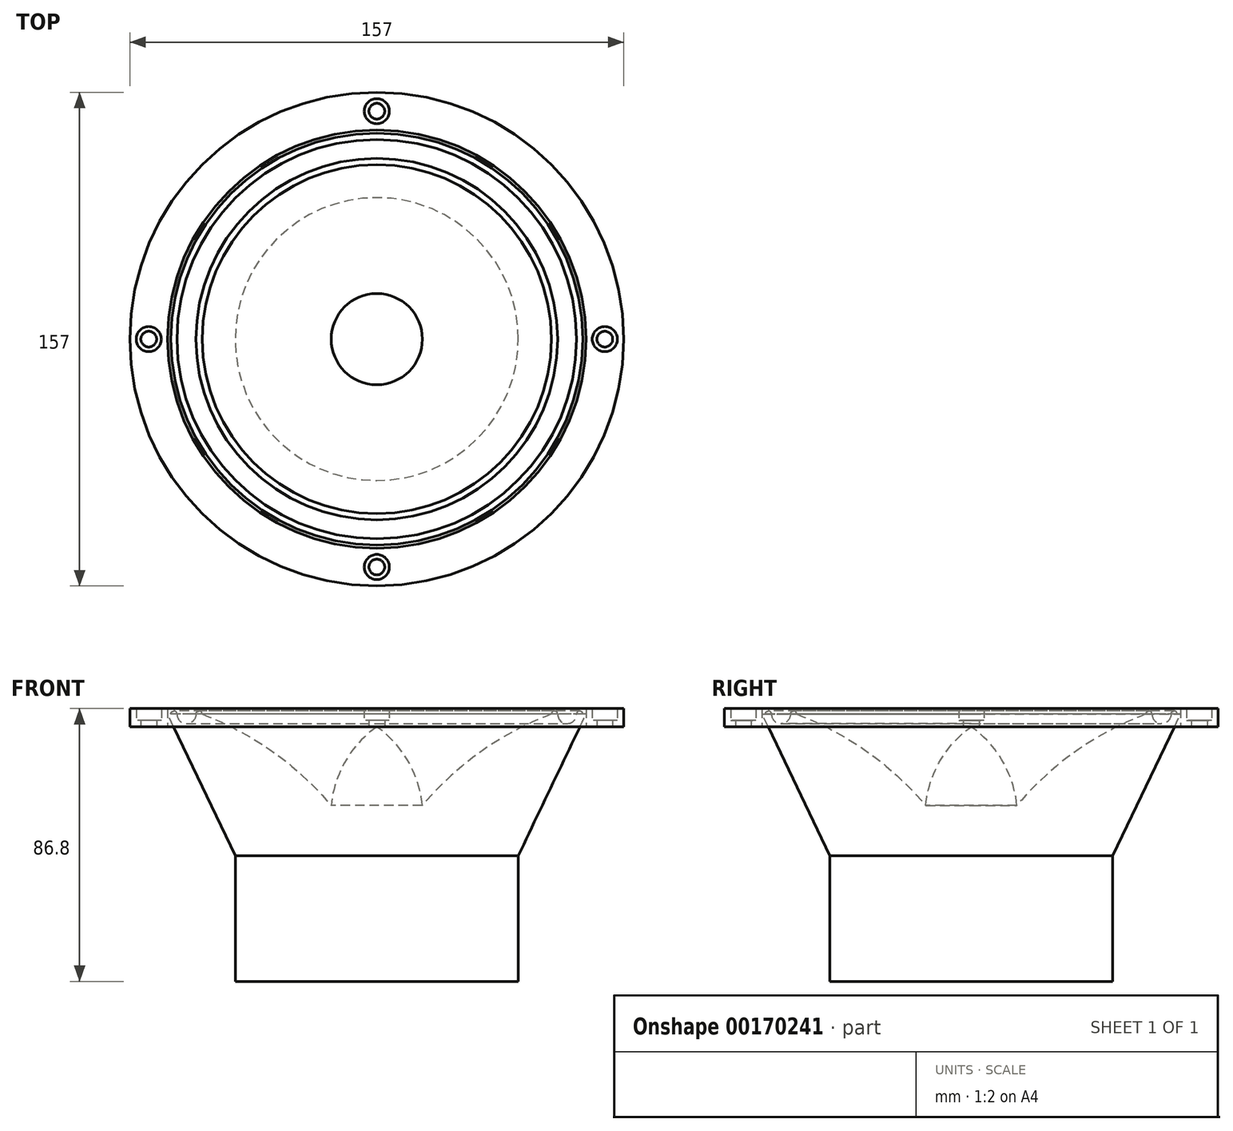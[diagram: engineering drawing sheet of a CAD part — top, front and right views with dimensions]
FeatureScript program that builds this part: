
annotation { "Feature Type Name" : "Feature", "Feature Type Description" : "" }
export const myFeature = defineFeature(function(context is Context, id is Id, definition is map)
    precondition{}
    {
        {
            var Q0;
            Q0=qCreatedBy(makeId("Top.planeOp"),FACE);
            var sketch = newSketch(context, id + "F0", { "sketchPlane" : qUnion([Q0])});
            skCircle(sketch, "E0", {"center": v(0, 0) * mm, "radius": 78.5 * mm});
            skCircle(sketch, "E1", {"center": v(0, 0) * mm, "radius": 72.5 * mm, "construction": true});
            skCircle(sketch, "E2", {"center": v(0, 0) * mm, "radius": 65.5 * mm});
            skCircle(sketch, "E3", {"center": v(0, 72.5) * mm, "radius": 2.5 * mm});
            skCircle(sketch, "E4", {"center": v(0, 72.5) * mm, "radius": 4 * mm});
            skLineSegment(sketch, "E5", {"start": v(0, 0) * mm, "end": v(0, 72.5) * mm, "construction": true});
            skCircle(sketch, "E6.1.0", {"center": v(-72.5, 0) * mm, "radius": 2.5 * mm});
            skCircle(sketch, "E6.1.1", {"center": v(-72.5, 0) * mm, "radius": 4 * mm});
            skCircle(sketch, "E6.2.0", {"center": v(0, -72.5) * mm, "radius": 2.5 * mm});
            skCircle(sketch, "E6.2.1", {"center": v(0, -72.5) * mm, "radius": 4 * mm});
            skCircle(sketch, "E7.1.3.0", {"center": v(72.5, 0) * mm, "radius": 2.5 * mm});
            skCircle(sketch, "E7.2.3.0", {"center": v(72.5, 0) * mm, "radius": 4 * mm});
            skLineSegment(sketch, "E8", {"start": v(0, 78.5) * mm, "end": v(0, 66.5) * mm, "construction": true});
            skCircle(sketch, "E9", {"center": v(0, 0) * mm, "radius": 66.5 * mm});
            skCircle(sketch, "E10", {"center": v(0, 0) * mm, "radius": 63.5 * mm});
            skCircle(sketch, "E11", {"center": v(0, 0) * mm, "radius": 57.5 * mm});
            skCircle(sketch, "E12", {"center": v(0, 0) * mm, "radius": 55.5 * mm});
            skCircle(sketch, "E13", {"center": v(0, 0) * mm, "radius": 14.5 * mm});
            skCircle(sketch, "E14", {"center": v(0, 0) * mm, "radius": 12.5 * mm});
            skSolve(sketch);
        }
        {
            var Q0;
            Q0=makeQuery(id+"F0.imprint","IMPRINT",FACE,{"disambiguationData":[TD([[makeQuery(id+"F0.imprint","IMPRINT",EDGE,{"derivedFrom":sQuery(id+"F0.wireOp",EDGE,"E0")}),1.0]])]});
            extrude(context, id + "F1", {"entities" : qUnion([Q0]), "depth" : 5.8 * mm});
        }
        {
            var Q0;
            Q0=makeQuery(id+"F0.imprint","IMPRINT",FACE,{"disambiguationData":[TD([[makeQuery(id+"F0.imprint","IMPRINT",EDGE,{"derivedFrom":sQuery(id+"F0.wireOp",EDGE,"E6.2.0")}),-1.0]])]});
            var Q1;
            Q1=makeQuery(id+"F0.imprint","IMPRINT",FACE,{"disambiguationData":[TD([[makeQuery(id+"F0.imprint","IMPRINT",EDGE,{"derivedFrom":sQuery(id+"F0.wireOp",EDGE,"E6.1.0")}),-1.0]])]});
            var Q2;
            Q2=makeQuery(id+"F0.imprint","IMPRINT",FACE,{"disambiguationData":[TD([[makeQuery(id+"F0.imprint","IMPRINT",EDGE,{"derivedFrom":sQuery(id+"F0.wireOp",EDGE,"E3")}),-1.0]])]});
            var Q3;
            Q3=makeQuery(id+"F0.imprint","IMPRINT",FACE,{"disambiguationData":[TD([[makeQuery(id+"F0.imprint","IMPRINT",EDGE,{"derivedFrom":sQuery(id+"F0.wireOp",EDGE,"E7.1.3.0")}),-1.0]])]});
            extrude(context, id + "F2", {"entities" : qUnion([Q0, Q1, Q2, Q3]), "operationType" : NewBodyOperationType.ADD, "depth" : 2 * mm});
        }
        {
            var Q0;
            Q0=qCreatedBy(makeId("Right.planeOp"),FACE);
            var sketch = newSketch(context, id + "F3", { "sketchPlane" : qUnion([Q0])});
            skLineSegment(sketch, "E15.0", {"start": v(-65.5, 0) * mm, "end": v(65.5, 0) * mm, "construction": true});
            skLineSegment(sketch, "E16.0", {"start": v(-63.5, 0) * mm, "end": v(63.5, 0) * mm, "construction": true});
            skLineSegment(sketch, "E17.0", {"start": v(-57.5, 0) * mm, "end": v(57.5, 0) * mm, "construction": true});
            skLineSegment(sketch, "E18.0", {"start": v(-55.5, 0) * mm, "end": v(55.5, 0) * mm, "construction": true});
            skLineSegment(sketch, "E19", {"start": v(-65.5, 0) * mm, "end": v(-65.5, 4) * mm, "construction": true});
            skLineSegment(sketch, "E20", {"start": v(-65.5, 4) * mm, "end": v(65.5, 4) * mm, "construction": true});
            skLineSegment(sketch, "E21", {"start": v(65.5, 4) * mm, "end": v(65.5, 0) * mm, "construction": true});
            skLineSegment(sketch, "E22", {"start": v(-63.5, 0) * mm, "end": v(-63.5, 4) * mm, "construction": true});
            skLineSegment(sketch, "E23", {"start": v(-57.5, 0) * mm, "end": v(-57.5, 4) * mm, "construction": true});
            skLineSegment(sketch, "E24", {"start": v(-55.5, 0) * mm, "end": v(-55.5, 4) * mm, "construction": true});
            skLineSegment(sketch, "E25", {"start": v(63.5, 0) * mm, "end": v(63.5, 4) * mm, "construction": true});
            skLineSegment(sketch, "E26", {"start": v(57.5, 0) * mm, "end": v(57.5, 4) * mm, "construction": true});
            skLineSegment(sketch, "E27", {"start": v(55.5, 0) * mm, "end": v(55.5, 4) * mm, "construction": true});
            skLineSegment(sketch, "E28.0", {"start": v(-14.5, 0) * mm, "end": v(14.5, 0) * mm});
            skLineSegment(sketch, "E29.0", {"start": v(-12.5, 0) * mm, "end": v(12.5, 0) * mm});
            skLineSegment(sketch, "E30", {"start": v(-14.5, 0) * mm, "end": v(-14.5, -25) * mm, "construction": true});
            skArc(sketch, "E31", {"start": v(-14.5, -25) * mm, "mid": v(-33.15, -7.88) * mm, "end": v(-55.5, 4) * mm});
            skArc(sketch, "E32", {"start": v(0, 0) * mm, "mid": v(-9.95, -10.93) * mm, "end": v(-14.5, -25) * mm});
            skLineSegment(sketch, "E33", {"start": v(0, 0) * mm, "end": v(0, -25) * mm});
            skLineSegment(sketch, "E34", {"start": v(0, -25) * mm, "end": v(-14.5, -25) * mm});
            skLineSegment(sketch, "E35.0", {"start": v(-66.5, 0) * mm, "end": v(66.5, 0) * mm, "construction": true});
            skLineSegment(sketch, "E36", {"start": v(-66.5, 4) * mm, "end": v(-45, -41) * mm});
            skLineSegment(sketch, "E37", {"start": v(-45, -41) * mm, "end": v(0, -41) * mm});
            skLineSegment(sketch, "E38", {"start": v(0, -41) * mm, "end": v(0, -25) * mm});
            skLineSegment(sketch, "E39", {"start": v(-65.5, 0) * mm, "end": v(-66.5, 0) * mm});
            skLineSegment(sketch, "E40", {"start": v(-45, -41) * mm, "end": v(-45, -81) * mm});
            skLineSegment(sketch, "E41", {"start": v(-45, -81) * mm, "end": v(0, -81) * mm});
            skLineSegment(sketch, "E42", {"start": v(0, -81) * mm, "end": v(0, -41) * mm});
            skLineSegment(sketch, "E43", {"start": v(-66.5, 4) * mm, "end": v(-65.5, 4) * mm});
            skArc(sketch, "E44", {"start": v(-63.5, 4) * mm, "mid": v(-64.5, 5) * mm, "end": v(-65.5, 4) * mm});
            skArc(sketch, "E45", {"start": v(-55.5, 4) * mm, "mid": v(-56.5, 5) * mm, "end": v(-57.5, 4) * mm});
            skArc(sketch, "E46", {"start": v(-63.5, 4) * mm, "mid": v(-60.5, 1) * mm, "end": v(-57.5, 4) * mm});
            skSolve(sketch);
        }
        {
            var Q0;
            Q0=makeQuery(id+"F3.imprint","IMPRINT",FACE,{"disambiguationData":[TD([[makeQuery(id+"F3.imprint","IMPRINT",EDGE,{"derivedFrom":sQuery(id+"F3.wireOp",EDGE,"E31")}),1.0]])]});
            var Q1;
            Q1=makeQuery(id+"F3.imprint","IMPRINT",FACE,{"disambiguationData":[TD([[makeQuery(id+"F3.imprint","IMPRINT",EDGE,{"derivedFrom":sQuery(id+"F3.wireOp",EDGE,"E37")}),-1.0]])]});
            var Q2;
            Q2=sQuery(id+"F3.wireOp",EDGE,"E33");
            revolve(context, id + "F4", {"entities" : qUnion([Q0, Q1]), "axis" : qUnion([Q2]), "revolveType" : RevolveType.FULL});
        }
        {
            var Q0;
            Q0=makeQuery(id+"F3.imprint","IMPRINT",FACE,{"disambiguationData":[TD([[makeQuery(id+"F3.imprint","IMPRINT",EDGE,{"derivedFrom":sQuery(id+"F3.wireOp",EDGE,"E32")}),1.0]])]});
            var Q1;
            Q1=sQuery(id+"F3.wireOp",EDGE,"E33");
            revolve(context, id + "F5", {"entities" : qUnion([Q0]), "axis" : qUnion([Q1]), "revolveType" : RevolveType.FULL});
        }
    });
